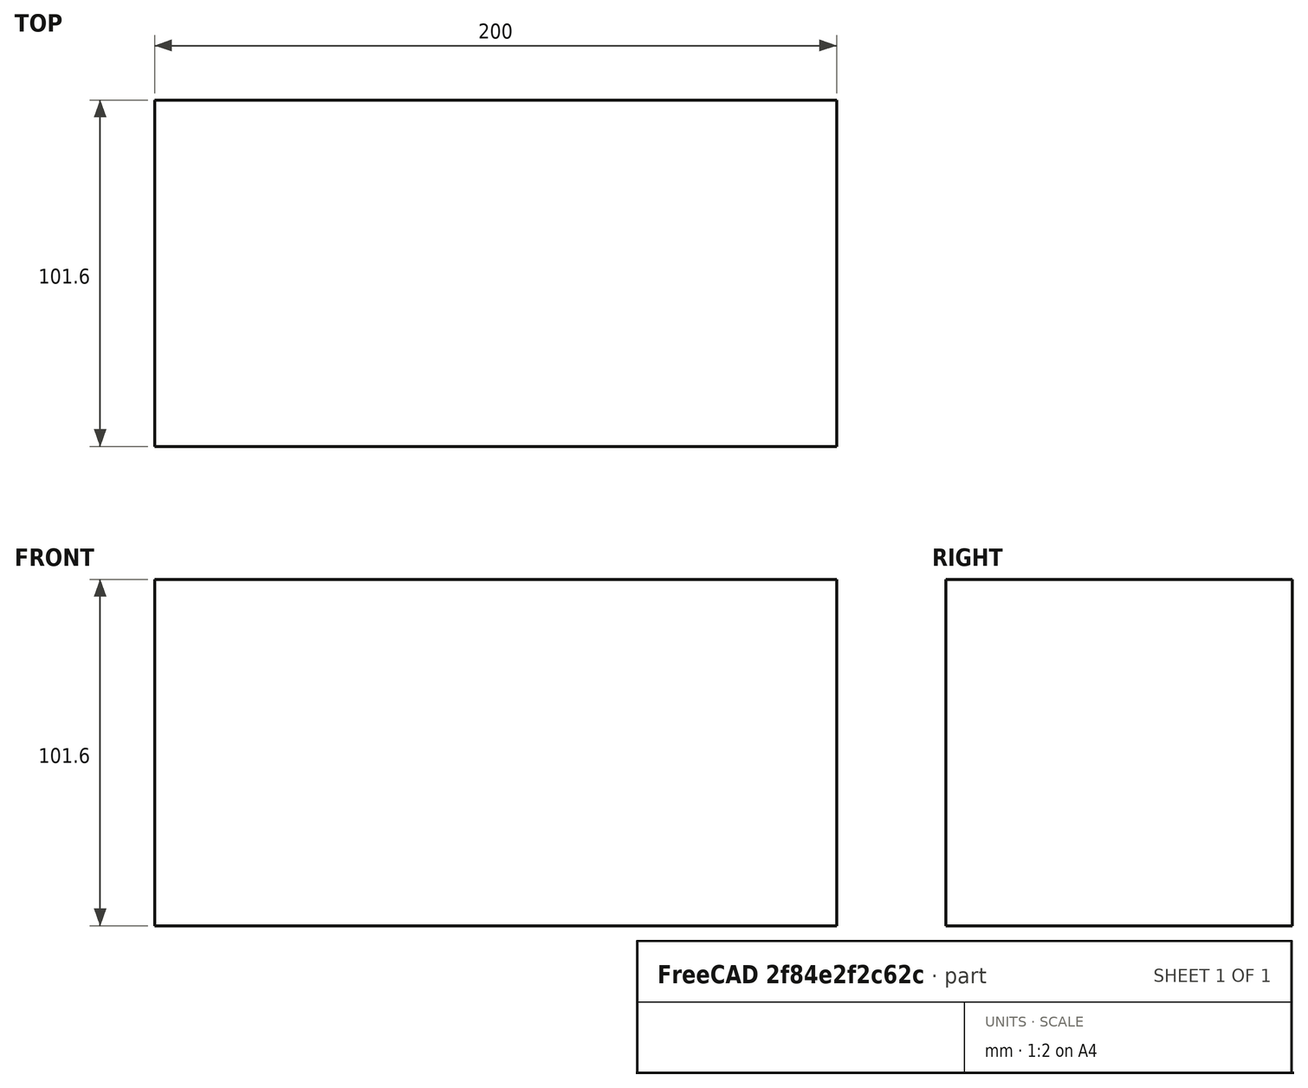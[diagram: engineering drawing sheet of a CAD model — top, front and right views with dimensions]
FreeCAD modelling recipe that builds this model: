
FCSTD DOCUMENT  (FreeCAD 1.0R39319 (Git))
Label: PartDesignDemo1
License: All rights reserved
LicenseURL: https://en.wikipedia.org/wiki/All_rights_reserved
objects: App::VarSet×2, App::Part×1, Sketcher::SketchObject×1, PartDesign::Pad×1, PartDesign::Body×1, App::FeaturePython×1
note: 6 computed .brp shape members not serialized (recipe doc carries the construction recipe); baked Part::Feature solids carry a one-line shape summary decoded from their .brp

FEATURE [App::Part] Part
  Origin = -> Origin001
FEATURE [Sketcher::SketchObject] Sketch
  ArcFitTolerance = 1e-06
  AttachmentSupport = -> [XY_Plane]
  FullyConstrained = true
  MakeInternals = false
  MapMode = 5
  expr: Constraints[10] = VarSet.Base_w
  expr: Constraints[9] = VarSet.Base_b
  sketch-geometry (4):
    g0: LineSegment StartX=0 StartY=101.6 StartZ=0 EndX=0 EndY=0 EndZ=0
    g1: LineSegment StartX=0 StartY=0 StartZ=0 EndX=200 EndY=0 EndZ=0
    g2: LineSegment StartX=200 StartY=0 StartZ=0 EndX=200 EndY=101.6 EndZ=0
    g3: LineSegment StartX=200 StartY=101.6 StartZ=0 EndX=0 EndY=101.6 EndZ=0
  constraints (11):
    c: Coincident(g0,g1)
    c: Coincident(g1,g2)
    c: Coincident(g2,g3)
    c: Coincident(g3,g0)
    c: Vertical(g0)
    c: Vertical(g2)
    c: Horizontal(g1)
    c: Horizontal(g3)
    c: Coincident(g0,g-1)
    c: DistanceX(g3,g3) = 200
    c: DistanceY(g2,g2) = 101.6
FEATURE [PartDesign::Pad] Pad
  Direction = (0,0,1)
  Length = 101.6
  Length2 = 10
  Profile = -> Sketch
  ReferenceAxis = -> Sketch [N_Axis]
  Refine = true
  Suppressed = false
  Type = 0
  expr: Length = VarSet.Base_w
FEATURE [PartDesign::Body] Body
  AllowCompound = false
  Group = -> [Sketch,Pad]
  Origin = -> Origin
  Tip = -> Pad
FEATURE [App::VarSet] VarSet  label="PQs"
  Base_H = 76.2
  Base_b = 200
  Base_d = 152.4
  Base_r = 76.2
  Base_w = 101.6
  expr: Base_r = Base_d / 2
FEATURE [App::VarSet] VarSet001  label="VS1"
  Base_A = 5806.44
  Base_x = 25.4
  Base_y = 76.2
  expr: Base_A = <<PQs>>.Base_r ^ 2
  expr: Base_y = <<PQs>>.Base_r
FEATURE [App::FeaturePython] CLParamHub  # WARN: FeaturePython — macro-defined, semantics opaque (R4)
  LastPushJSON = {\n  "docName": "PartDesignDemo1",\n  "docFile": "<userpath>/AppData/Roaming/FreeCAD/Mod/CalcsLiveWorkbench/models/PartDesignDemo1.FCStd",\n  "params": []\n}
  MappingJSON = {\n  "docVersion": "0.1",\n  "unitsSchema": "UserPreferred",\n  "params": []\n}
